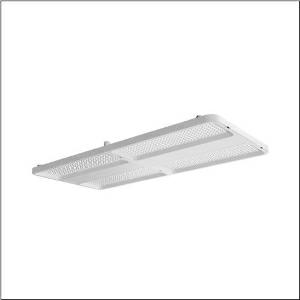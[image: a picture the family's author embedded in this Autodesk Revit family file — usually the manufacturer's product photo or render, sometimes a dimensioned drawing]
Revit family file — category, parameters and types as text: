
# Revit family: highbay_11_maxi_51hn11db4qda
name_source: partatom
category: Lighting Fixtures
units: mm (PartAtom-declared; Revit-internal decimal feet)

## family parameters
Cut with Voids When Loaded = No
Host = Face
Light Source = No
Part Type = Normal
Room Calculation Point = No
Round Connector Dimension = Use Diameter
Shared = No

## types (1)
- --- (1 x LED, 5620 lm, 27.8 W, 4000K)
    Apparent Load = 28 VA
    CIE Flux Codes = 85 97 100 100 100
    Color Rendering = 80
    Color Temperature = 4000K
    Default Elevation = 1800 mm
    Description = high bay luminaire Highbay 11 maxi; direct symmetric narrow distribution, light control with lens of PMMA; UGR ≤ 22 (X = 4H | Y = 8H | S = 0.25H | reflection values 70/50/20); luminous flux: 36.000lm; light colour: 840, colour temperature: 4000K, MacAdam ≤ 2 SDCM (initial), colour rendering: CRI > 80; luminous efficacy: 202,6lm/W; rated service life: 100.000h (L95/B50) at AT= 25°C; control: DALI 2; housing frame of high-performance plastic PA6, matt traffic white (RAL 9016); cover of PMMA; dimension (LxWxH): 946 x 442 x 72mm; luminaire connection: terminal, 5-pole, max. 2.5mm² (cable entry for one cable, Ø 8.5..16mm); mains connection: 230..240V, AC/DC 0/50..60Hz; connected load: 177,7W; protection rating (complete): IP66; insulation class (complete): insulation class I (protective earthing); protection symbol: D; impact resistance: IK08; halogen-free wiring; for central battery installations according to DIN EN 60598-2-22; corresponds to IFS (International Featured Standards) requirements for safety and quality in the food industry; LABS conformity tested according to VDMA 24364:2018-05; certification: CE, ENEC, VDE, UKCA; permissible operating ambient temperature: -40..+55°C (reducing of maximum allowable ambient temperature of 5°C with ceiling mounting); packaging unit: 1 piece; (delivery without accessories; please order mounting accessories separately)
    Height = 72 mm  [stored 0.23622 ft]
    Lamp = 1 x LED
    Lamp Light Flux = 5620 lm
    Lamp Power = 27.8 W
    Lamp count = 1
    Length = 946 mm
    Luminous efficacy = 202 lm/W
    Manufacturer = Siteco
    ModVariant = No
    Model = 51HN11DB4QDA
    Mounting Place = Ceiling
    Mounting Type = Pendant
    Number of Poles = 1
    OnlyDefault = Yes
    Power Factor = 1
    Product Name = Highbay 11 maxi
    Product group = high bay luminaire
    ProductGroupID = 901
    Protection Class = Protection class I
    Protection Degree = IP 66
    RLX_Detail_Level = 1
    RLX_Emergency_Light_Flux = 0 lm
    RLX_Emergency_Type = 0
    RLX_Emergency_Type_DB = No
    RlxData = <blob elided: 22341 chars, md5=df6d1404>
    Socket = socket
    Standby Power = 0 W
    System Light Flux = 5620 lm
    System Power = 28 W
    Type Comments = : DC mode (central or group accumulator) initial emergency light level
    Type Image = l_1363244.jpg
    URL = http://relux.com
    VarID = @adj_003705
    Voltage = 0 V
    Weight = 0.00 kg
    Width = 442 mm

note: [stored X ft] marks values corroborated as IEEE doubles in the binary element streams (Revit-internal decimal feet)

## geometry (parser evidence)
native form markers: Blend x4, Sweep x12
no freeform markers — native parametric forms only
